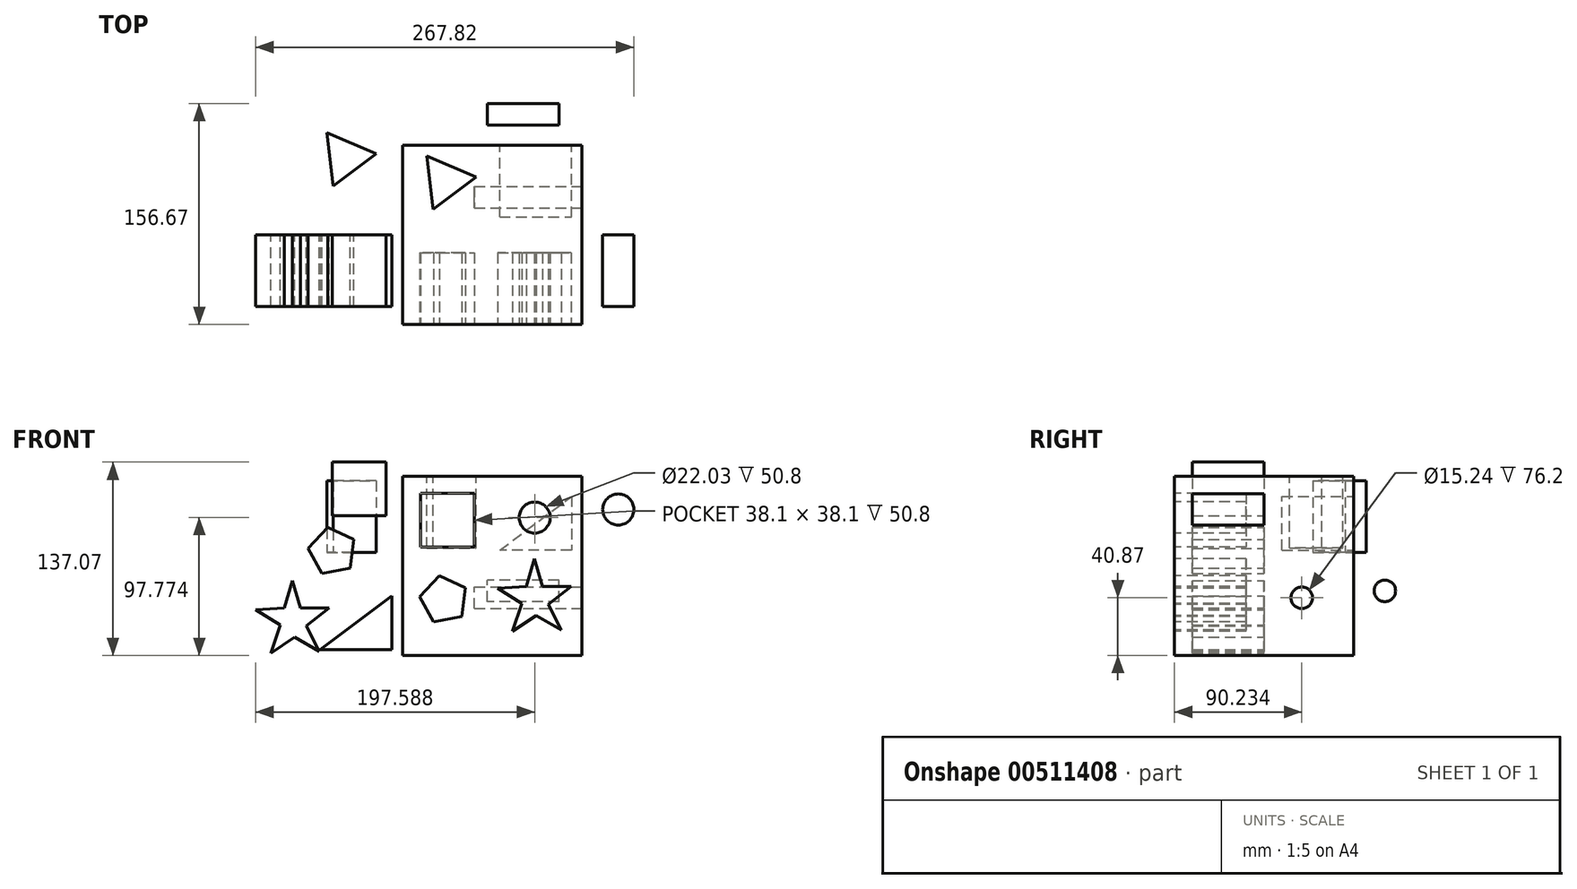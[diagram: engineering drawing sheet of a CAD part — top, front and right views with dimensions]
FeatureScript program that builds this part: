
annotation { "Feature Type Name" : "Feature", "Feature Type Description" : "" }
export const myFeature = defineFeature(function(context is Context, id is Id, definition is map)
    precondition{}
    {
        {
            var Q0;
            Q0=qCreatedBy(makeId("Front.planeOp"),FACE);
            var sketch = newSketch(context, id + "F0", { "sketchPlane" : qUnion([Q0])});
            skLineSegment(sketch, "E0.bottom", {"start": v(-59.97, 54.05) * mm, "end": v(67.03, 54.05) * mm});
            skLineSegment(sketch, "E0.top", {"start": v(-59.97, -72.95) * mm, "end": v(67.03, -72.95) * mm});
            skLineSegment(sketch, "E0.left", {"start": v(-59.97, 54.05) * mm, "end": v(-59.97, -72.95) * mm});
            skLineSegment(sketch, "E0.right", {"start": v(67.03, 54.05) * mm, "end": v(67.03, -72.95) * mm});
            skSolve(sketch);
        }
        {
            var Q0;
            Q0 = qSketchRegion(id + "F0", true);
            extrude(context, id + "F1", {"entities" : qUnion([Q0]), "endBound" : BoundingType.SYMMETRIC, "depth" : 127 * mm});
        }
        {
            var Q0;
            Q0=makeQuery(id+"F1.opExtrude","CAP_FACE",FACE,{"disambiguationData":[OSD([sQuery(id+"F0.wireOp",EDGE,"E0.bottom"),sQuery(id+"F0.wireOp",EDGE,"E0.top"),sQuery(id+"F0.wireOp",EDGE,"E0.left"),sQuery(id+"F0.wireOp",EDGE,"E0.right")])],"isStart":false});
            var sketch = newSketch(context, id + "F2", { "sketchPlane" : qUnion([Q0])});
            skLineSegment(sketch, "E1.bottom", {"start": v(-47.12, 42) * mm, "end": v(-9.02, 42) * mm});
            skLineSegment(sketch, "E1.top", {"start": v(-47.12, 3.9) * mm, "end": v(-9.02, 3.9) * mm});
            skLineSegment(sketch, "E1.left", {"start": v(-47.12, 42) * mm, "end": v(-47.12, 3.9) * mm});
            skLineSegment(sketch, "E1.right", {"start": v(-9.02, 42) * mm, "end": v(-9.02, 3.9) * mm});
            skSolve(sketch);
        }
        {
            var Q0;
            Q0=makeQuery(id+"F2.imprint","IMPRINT",FACE,{"disambiguationData":[TD([[makeQuery(id+"F2.imprint","IMPRINT",EDGE,{"derivedFrom":sQuery(id+"F2.wireOp",EDGE,"E1.bottom")}),-1.0]])]});
            extrude(context, id + "F3", {"entities" : qUnion([Q0]), "operationType" : NewBodyOperationType.REMOVE, "oppositeDirection" : true, "depth" : 50.8 * mm});
        }
        {
            var Q0;
            Q0=makeQuery(id+"F1.opExtrude","CAP_FACE",FACE,{"disambiguationData":[OSD([sQuery(id+"F0.wireOp",EDGE,"E0.bottom"),sQuery(id+"F0.wireOp",EDGE,"E0.top"),sQuery(id+"F0.wireOp",EDGE,"E0.left"),sQuery(id+"F0.wireOp",EDGE,"E0.right")])],"isStart":false});
            var sketch = newSketch(context, id + "F4", { "sketchPlane" : qUnion([Q0])});
            skCircle(sketch, "E2", {"center": v(33.6, 24.82) * mm, "radius": 11.02 * mm});
            skSolve(sketch);
        }
        {
            var Q0;
            Q0=makeQuery(id+"F4.imprint","IMPRINT",FACE,{"disambiguationData":[TD([[makeQuery(id+"F4.imprint","IMPRINT",EDGE,{"derivedFrom":sQuery(id+"F4.wireOp",EDGE,"E2")}),1.0]])]});
            extrude(context, id + "F5", {"entities" : qUnion([Q0]), "operationType" : NewBodyOperationType.REMOVE, "oppositeDirection" : true, "depth" : 50.8 * mm});
        }
        {
            var Q0;
            Q0=makeQuery(id+"F1.opExtrude","CAP_FACE",FACE,{"disambiguationData":[OSD([sQuery(id+"F0.wireOp",EDGE,"E0.bottom"),sQuery(id+"F0.wireOp",EDGE,"E0.top"),sQuery(id+"F0.wireOp",EDGE,"E0.left"),sQuery(id+"F0.wireOp",EDGE,"E0.right")])],"isStart":false});
            var sketch = newSketch(context, id + "F6", { "sketchPlane" : qUnion([Q0])});
            skCircle(sketch, "E3.cCircle", {"center": v(-30.74, -33.42) * mm, "radius": 17.29 * mm, "construction": true});
            skLineSegment(sketch, "E3.0", {"start": v(-18.11, -45.22) * mm, "end": v(-38.06, -49.08) * mm});
            skLineSegment(sketch, "E3.1", {"start": v(-38.06, -49.08) * mm, "end": v(-47.9, -31.3) * mm});
            skLineSegment(sketch, "E3.2", {"start": v(-47.9, -31.3) * mm, "end": v(-34.03, -16.45) * mm});
            skLineSegment(sketch, "E3.3", {"start": v(-34.03, -16.45) * mm, "end": v(-15.62, -25.05) * mm});
            skLineSegment(sketch, "E3.4", {"start": v(-15.62, -25.05) * mm, "end": v(-18.11, -45.22) * mm});
            skSolve(sketch);
        }
        {
            var Q0;
            Q0 = qSketchRegion(id + "F6", true);
            extrude(context, id + "F7", {"entities" : qUnion([Q0]), "operationType" : NewBodyOperationType.REMOVE, "oppositeDirection" : true, "depth" : 50.8 * mm});
        }
        {
            var Q0;
            Q0=makeQuery(id+"F1.opExtrude","CAP_FACE",FACE,{"disambiguationData":[OSD([sQuery(id+"F0.wireOp",EDGE,"E0.bottom"),sQuery(id+"F0.wireOp",EDGE,"E0.top"),sQuery(id+"F0.wireOp",EDGE,"E0.left"),sQuery(id+"F0.wireOp",EDGE,"E0.right")])],"isStart":false});
            var sketch = newSketch(context, id + "F8", { "sketchPlane" : qUnion([Q0])});
            skLineSegment(sketch, "E4", {"start": v(27.69, -23.95) * mm, "end": v(33.48, -4.47) * mm});
            skLineSegment(sketch, "E5", {"start": v(33.48, -4.47) * mm, "end": v(38.98, -24.04) * mm});
            skLineSegment(sketch, "E6", {"start": v(38.98, -24.04) * mm, "end": v(59.3, -24.04) * mm});
            skLineSegment(sketch, "E7", {"start": v(59.3, -24.04) * mm, "end": v(43.32, -36.59) * mm});
            skLineSegment(sketch, "E8", {"start": v(43.32, -36.59) * mm, "end": v(52.32, -54.8) * mm});
            skLineSegment(sketch, "E9", {"start": v(52.32, -54.8) * mm, "end": v(34.77, -44.56) * mm});
            skLineSegment(sketch, "E10", {"start": v(34.77, -44.56) * mm, "end": v(17.95, -55.95) * mm});
            skLineSegment(sketch, "E11", {"start": v(17.95, -55.95) * mm, "end": v(24.62, -36.16) * mm});
            skLineSegment(sketch, "E12", {"start": v(24.62, -36.16) * mm, "end": v(7.41, -25.35) * mm});
            skLineSegment(sketch, "E13", {"start": v(7.41, -25.35) * mm, "end": v(27.69, -23.95) * mm});
            skSolve(sketch);
        }
        {
            var Q0;
            Q0=makeQuery(id+"F1.opExtrude","SWEPT_FACE",FACE,{"disambiguationData":[OSD([sQuery(id+"F0.wireOp",EDGE,"E0.bottom")])]});
            var sketch = newSketch(context, id + "F9", { "sketchPlane" : qUnion([Q0])});
            skCircle(sketch, "E14.cCircle", {"center": v(-29.67, 38.25) * mm, "radius": 11 * mm, "construction": true});
            skLineSegment(sketch, "E14.0", {"start": v(-7.83, 40.89) * mm, "end": v(-38.31, 18.03) * mm});
            skLineSegment(sketch, "E14.1", {"start": v(-38.31, 18.03) * mm, "end": v(-42.87, 55.85) * mm});
            skLineSegment(sketch, "E14.2", {"start": v(-42.87, 55.85) * mm, "end": v(-7.83, 40.89) * mm});
            skPoint(sketch, "E14.0.midPoint", {"position": v(-23.07, 29.46) * mm});
            skSolve(sketch);
        }
        {
            var Q0;
            Q0 = qSketchRegion(id + "F9", true);
            extrude(context, id + "F10", {"entities" : qUnion([Q0]), "operationType" : NewBodyOperationType.REMOVE, "oppositeDirection" : true, "depth" : 50.8 * mm});
        }
        {
            var Q0;
            Q0=makeQuery(id+"F1.opExtrude","SWEPT_FACE",FACE,{"disambiguationData":[OSD([sQuery(id+"F0.wireOp",EDGE,"E0.right")])]});
            var sketch = newSketch(context, id + "F11", { "sketchPlane" : qUnion([Q0])});
            skCircle(sketch, "E15", {"center": v(26.73, -32.08) * mm, "radius": 7.62 * mm});
            skSolve(sketch);
        }
        {
            var Q0;
            Q0=makeQuery(id+"F11.imprint","IMPRINT",FACE,{"disambiguationData":[TD([[makeQuery(id+"F11.imprint","IMPRINT",EDGE,{"derivedFrom":sQuery(id+"F11.wireOp",EDGE,"E15")}),1.0]])]});
            extrude(context, id + "F12", {"entities" : qUnion([Q0]), "operationType" : NewBodyOperationType.REMOVE, "oppositeDirection" : true, "depth" : 76.2 * mm});
        }
        {
            var Q0;
            Q0 = qSketchRegion(id + "F8", true);
            extrude(context, id + "F13", {"entities" : qUnion([Q0]), "operationType" : NewBodyOperationType.REMOVE, "oppositeDirection" : true, "depth" : 50.8 * mm});
        }
        {
            var Q0;
            Q0=makeQuery(id+"F1.opExtrude","CAP_FACE",FACE,{"disambiguationData":[OSD([sQuery(id+"F0.wireOp",EDGE,"E0.bottom"),sQuery(id+"F0.wireOp",EDGE,"E0.top"),sQuery(id+"F0.wireOp",EDGE,"E0.left"),sQuery(id+"F0.wireOp",EDGE,"E0.right")])],"isStart":true});
            var sketch = newSketch(context, id + "F14", { "sketchPlane" : qUnion([Q0])});
            skLineSegment(sketch, "E16", {"start": v(-59.67, 39.86) * mm, "end": v(-59.67, 1.76) * mm});
            skLineSegment(sketch, "E17", {"start": v(-59.67, 1.76) * mm, "end": v(-8.87, 1.76) * mm});
            skLineSegment(sketch, "E18", {"start": v(-8.87, 1.76) * mm, "end": v(-59.67, 39.86) * mm});
            skSolve(sketch);
        }
        {
            var Q0;
            Q0 = qSketchRegion(id + "F14", true);
            extrude(context, id + "F15", {"entities" : qUnion([Q0]), "operationType" : NewBodyOperationType.REMOVE, "oppositeDirection" : true, "depth" : 50.8 * mm});
        }
        {
            var Q0;
            Q0=qCreatedBy(makeId("Front.planeOp"),FACE);
            var sketch = newSketch(context, id + "F16", { "sketchPlane" : qUnion([Q0])});
            skLineSegment(sketch, "E19.bottom", {"start": v(-109.75, 64.12) * mm, "end": v(-71.65, 64.12) * mm});
            skLineSegment(sketch, "E19.top", {"start": v(-109.75, 26.02) * mm, "end": v(-71.65, 26.02) * mm});
            skLineSegment(sketch, "E19.left", {"start": v(-109.75, 64.12) * mm, "end": v(-109.75, 26.02) * mm});
            skLineSegment(sketch, "E19.right", {"start": v(-71.65, 64.12) * mm, "end": v(-71.65, 26.02) * mm});
            skSolve(sketch);
        }
        {
            var Q0;
            Q0=makeQuery(id+"F16.imprint","IMPRINT",FACE,{"disambiguationData":[TD([[makeQuery(id+"F16.imprint","IMPRINT",EDGE,{"derivedFrom":sQuery(id+"F16.wireOp",EDGE,"E19.bottom")}),-1.0]])]});
            extrude(context, id + "F17", {"entities" : qUnion([Q0]), "depth" : 50.8 * mm});
        }
        {
            var Q0;
            Q0=qCreatedBy(makeId("Front.planeOp"),FACE);
            var sketch = newSketch(context, id + "F18", { "sketchPlane" : qUnion([Q0])});
            skCircle(sketch, "E20", {"center": v(92.82, 30.55) * mm, "radius": 11.02 * mm});
            skSolve(sketch);
        }
        {
            var Q0;
            Q0 = qSketchRegion(id + "F18", true);
            extrude(context, id + "F19", {"entities" : qUnion([Q0]), "depth" : 50.8 * mm, "offsetDistance" : 25.4 * mm});
        }
        {
            var Q0;
            Q0=qCreatedBy(makeId("Front.planeOp"),FACE);
            var sketch = newSketch(context, id + "F20", { "sketchPlane" : qUnion([Q0])});
            skCircle(sketch, "E21.cCircle", {"center": v(-109.64, 0.87) * mm, "radius": 17.29 * mm, "construction": true});
            skLineSegment(sketch, "E21.0", {"start": v(-97, -10.93) * mm, "end": v(-116.96, -14.79) * mm});
            skLineSegment(sketch, "E21.1", {"start": v(-116.96, -14.79) * mm, "end": v(-126.8, 3) * mm});
            skLineSegment(sketch, "E21.2", {"start": v(-126.8, 3) * mm, "end": v(-112.92, 17.84) * mm});
            skLineSegment(sketch, "E21.3", {"start": v(-112.92, 17.84) * mm, "end": v(-94.51, 9.24) * mm});
            skLineSegment(sketch, "E21.4", {"start": v(-94.51, 9.24) * mm, "end": v(-97, -10.93) * mm});
            skSolve(sketch);
        }
        {
            var Q0;
            Q0=qCreatedBy(makeId("Front.planeOp"),FACE);
            var sketch = newSketch(context, id + "F21", { "sketchPlane" : qUnion([Q0])});
            skLineSegment(sketch, "E22", {"start": v(-143.7, -39.28) * mm, "end": v(-137.91, -19.8) * mm});
            skLineSegment(sketch, "E23", {"start": v(-137.91, -19.8) * mm, "end": v(-132.41, -39.36) * mm});
            skLineSegment(sketch, "E24", {"start": v(-132.41, -39.36) * mm, "end": v(-112.1, -39.36) * mm});
            skLineSegment(sketch, "E25", {"start": v(-112.1, -39.36) * mm, "end": v(-128.07, -51.91) * mm});
            skLineSegment(sketch, "E26", {"start": v(-128.07, -51.91) * mm, "end": v(-119.07, -70.13) * mm});
            skLineSegment(sketch, "E27", {"start": v(-119.07, -70.13) * mm, "end": v(-136.62, -59.88) * mm});
            skLineSegment(sketch, "E28", {"start": v(-136.62, -59.88) * mm, "end": v(-153.45, -71.27) * mm});
            skLineSegment(sketch, "E29", {"start": v(-153.45, -71.27) * mm, "end": v(-146.78, -51.49) * mm});
            skLineSegment(sketch, "E30", {"start": v(-146.78, -51.49) * mm, "end": v(-163.98, -40.68) * mm});
            skLineSegment(sketch, "E31", {"start": v(-163.98, -40.68) * mm, "end": v(-143.7, -39.28) * mm});
            skSolve(sketch);
        }
        {
            var Q0;
            Q0=qCreatedBy(makeId("Right.planeOp"),FACE);
            var sketch = newSketch(context, id + "F22", { "sketchPlane" : qUnion([Q0])});
            skCircle(sketch, "E32", {"center": v(85.55, -27.12) * mm, "radius": 7.62 * mm});
            skSolve(sketch);
        }
        {
            var Q0;
            Q0 = qSketchRegion(id + "F22", true);
            extrude(context, id + "F23", {"entities" : qUnion([Q0]), "depth" : 50.8 * mm, "offsetDistance" : 25.4 * mm});
        }
        {
            var Q0;
            Q0=qCreatedBy(makeId("Top.planeOp"),FACE);
            var sketch = newSketch(context, id + "F24", { "sketchPlane" : qUnion([Q0])});
            skCircle(sketch, "E33.cCircle", {"center": v(-100.37, 54.85) * mm, "radius": 11 * mm, "construction": true});
            skLineSegment(sketch, "E33.0", {"start": v(-78.53, 57.48) * mm, "end": v(-109.01, 34.62) * mm});
            skLineSegment(sketch, "E33.1", {"start": v(-109.01, 34.62) * mm, "end": v(-113.57, 72.45) * mm});
            skLineSegment(sketch, "E33.2", {"start": v(-113.57, 72.45) * mm, "end": v(-78.53, 57.48) * mm});
            skPoint(sketch, "E33.0.midPoint", {"position": v(-93.77, 46.05) * mm});
            skSolve(sketch);
        }
        {
            var Q0;
            Q0 = qSketchRegion(id + "F24", true);
            extrude(context, id + "F25", {"entities" : qUnion([Q0]), "depth" : 50.8 * mm, "offsetDistance" : 25.4 * mm});
        }
        {
            var Q0;
            Q0=qCreatedBy(makeId("Front.planeOp"),FACE);
            var sketch = newSketch(context, id + "F26", { "sketchPlane" : qUnion([Q0])});
            skLineSegment(sketch, "E34", {"start": v(-67.48, -30.6) * mm, "end": v(-67.48, -68.7) * mm});
            skLineSegment(sketch, "E35", {"start": v(-67.48, -68.7) * mm, "end": v(-118.28, -68.7) * mm});
            skLineSegment(sketch, "E36", {"start": v(-118.28, -68.7) * mm, "end": v(-67.48, -30.6) * mm});
            skSolve(sketch);
        }
        {
            var Q0;
            Q0 = qSketchRegion(id + "F26", true);
            extrude(context, id + "F27", {"entities" : qUnion([Q0]), "depth" : 50.8 * mm, "offsetDistance" : 25.4 * mm});
        }
        {
            var Q0;
            Q0 = qSketchRegion(id + "F21", true);
            extrude(context, id + "F28", {"entities" : qUnion([Q0]), "depth" : 50.8 * mm, "offsetDistance" : 25.4 * mm});
        }
        {
            var Q0;
            Q0 = qSketchRegion(id + "F20", true);
            extrude(context, id + "F29", {"entities" : qUnion([Q0]), "depth" : 50.8 * mm, "offsetDistance" : 25.4 * mm});
        }
    });
